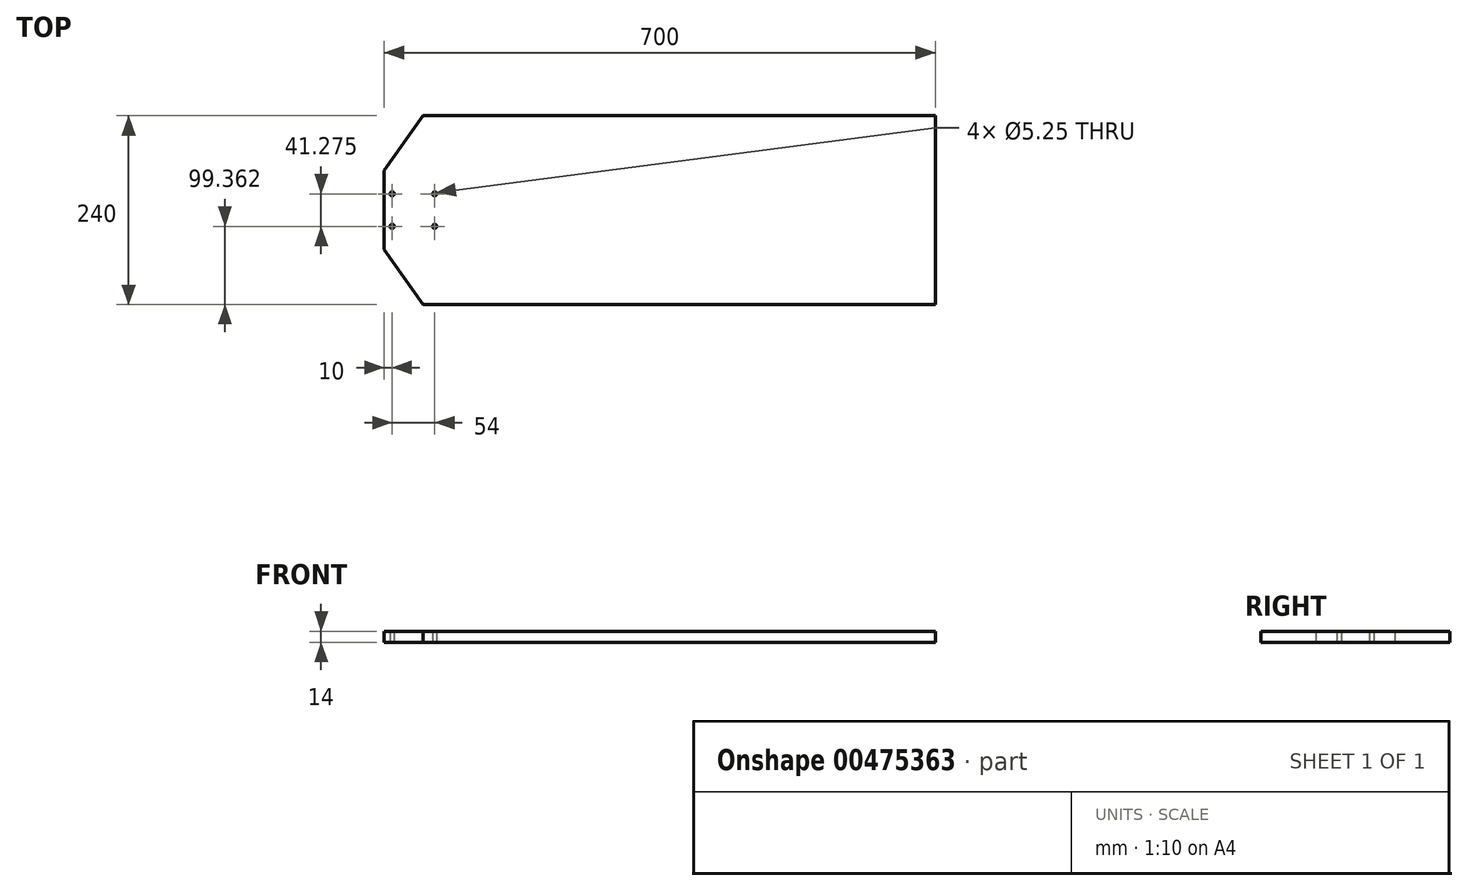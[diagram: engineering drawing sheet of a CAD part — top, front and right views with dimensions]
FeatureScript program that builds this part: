
annotation { "Feature Type Name" : "Feature", "Feature Type Description" : "" }
export const myFeature = defineFeature(function(context is Context, id is Id, definition is map)
    precondition{}
    {
        {
            var Q0;
            Q0=qCreatedBy(makeId("Top.planeOp"),FACE);
            var sketch = newSketch(context, id + "F0", { "sketchPlane" : qUnion([Q0])});
            skLineSegment(sketch, "E0.bottom", {"start": v(350, -120) * mm, "end": v(-350, -120) * mm});
            skLineSegment(sketch, "E0.top", {"start": v(350, 120) * mm, "end": v(-350, 120) * mm});
            skLineSegment(sketch, "E0.left", {"start": v(350, -120) * mm, "end": v(350, 120) * mm});
            skLineSegment(sketch, "E0.right", {"start": v(-350, -120) * mm, "end": v(-350, 120) * mm});
            skPoint(sketch, "E0.middle", {"position": v(0, 0) * mm});
            skPoint(sketch, "E1", {"position": v(-350, 0) * mm});
            skPoint(sketch, "E2", {"position": v(-350, 50) * mm});
            skLineSegment(sketch, "E3", {"start": v(-350, 50) * mm, "end": v(-300.99, 120) * mm});
            skPoint(sketch, "E4", {"position": v(-340, 0) * mm});
            skPoint(sketch, "E5", {"position": v(-340, 20.64) * mm});
            skPoint(sketch, "E6", {"position": v(-340, -20.64) * mm});
            skPoint(sketch, "E7", {"position": v(-286, 20.64) * mm});
            skPoint(sketch, "E8", {"position": v(-286, -20.64) * mm});
            skPoint(sketch, "E9", {"position": v(-350, -50) * mm});
            skLineSegment(sketch, "E10", {"start": v(-350, -50) * mm, "end": v(-300.99, -120) * mm});
            skSolve(sketch);
        }
        {
            var Q0;
            {var subQ3=sQuery(id+"F0.wireOp",EDGE,"E0.left");Q0=makeQuery(id+"F0.imprint","IMPRINT",FACE,{"disambiguationData":[TD([[makeQuery(id+"F0.imprint","IMPRINT",EDGE,{"derivedFrom":subQ3}),1.0]])]});}
            extrude(context, id + "F1", {"entities" : qUnion([Q0]), "depth" : 14 * mm});
        }
        {
            var Q0;
            Q0=sQuery(id+"F0.wireOp",VERTEX,"E5");
            var Q1;
            Q1=sQuery(id+"F0.wireOp",VERTEX,"E7");
            var Q2;
            Q2=sQuery(id+"F0.wireOp",VERTEX,"E8");
            var Q3;
            Q3=sQuery(id+"F0.wireOp",VERTEX,"E6");
            var Q4;
            Q4=makeQuery(id+"F1.opExtrude","SWEPT_BODY",BODY,{"disambiguationData":[OSD([sQuery(id+"F0.wireOp",EDGE,"E0.bottom"),sQuery(id+"F0.wireOp",EDGE,"E0.top"),sQuery(id+"F0.wireOp",EDGE,"E0.left"),sQuery(id+"F0.wireOp",EDGE,"E0.right"),sQuery(id+"F0.wireOp",EDGE,"E3"),sQuery(id+"F0.wireOp",EDGE,"E10")])]});
            hole(context, id + "F2", {"style" : HoleStyle.SIMPLE, "endStyle" : HoleEndStyle.THROUGH, "oppositeDirection" : true, "standardTappedOrClearance" : lookupTablePath({ "standard" : "ISO", "fit" : "Close", "size" : "M5", "type" : "Clearance" }), "standardBlindInLast" : lookupTablePath({ "fit" : "Close", "standard" : "ISO", "size" : "M5", "type" : "Clearance" }), "holeDiameter" : 5.25 * mm, "isTappedThrough" : true, "tappedDepth" : 12 * mm, "tapClearance" : 3, "locations" : qUnion([Q0, Q1, Q2, Q3]), "scope" : qUnion([Q4])});
        }
    });
